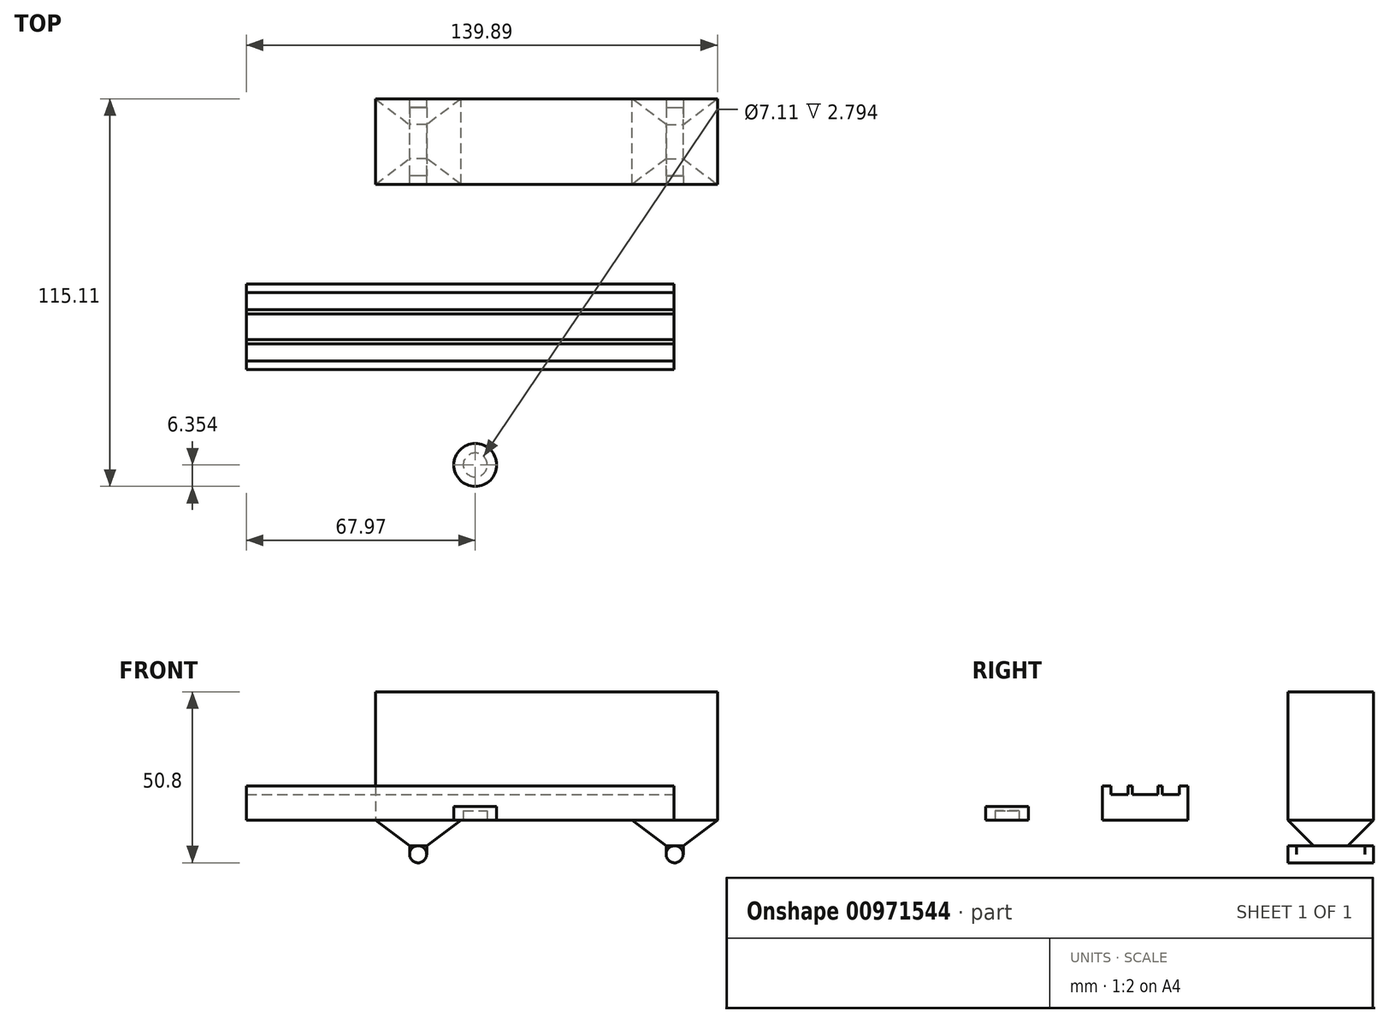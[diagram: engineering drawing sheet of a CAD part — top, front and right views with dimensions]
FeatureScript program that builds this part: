
annotation { "Feature Type Name" : "Feature", "Feature Type Description" : "" }
export const myFeature = defineFeature(function(context is Context, id is Id, definition is map)
    precondition{}
    {
        {
            var Q0;
            Q0=qCreatedBy(makeId("Top.planeOp"),FACE);
            var sketch = newSketch(context, id + "F0", { "sketchPlane" : qUnion([Q0])});
            skLineSegment(sketch, "E0.bottom", {"start": v(-67.97, 12.42) * mm, "end": v(59.03, 12.42) * mm});
            skLineSegment(sketch, "E0.top", {"start": v(-67.97, -12.98) * mm, "end": v(59.03, -12.98) * mm});
            skLineSegment(sketch, "E0.left", {"start": v(-67.97, 12.42) * mm, "end": v(-67.97, -12.98) * mm});
            skLineSegment(sketch, "E0.right", {"start": v(59.03, 12.42) * mm, "end": v(59.03, -12.98) * mm});
            skSolve(sketch);
        }
        {
            var Q0;
            Q0=makeQuery(id+"F0.imprint","IMPRINT",FACE,{"disambiguationData":[TD([[makeQuery(id+"F0.imprint","IMPRINT",EDGE,{"derivedFrom":sQuery(id+"F0.wireOp",EDGE,"E0.bottom")}),-1.0]])]});
            extrude(context, id + "F1", {"entities" : qUnion([Q0]), "depth" : 7.62 * mm, "offsetDistance" : 25.4 * mm});
        }
        {
            var Q0;
            Q0=makeQuery(id+"F1.opExtrude","CAP_FACE",FACE,{"disambiguationData":[OSD([sQuery(id+"F0.wireOp",EDGE,"E0.bottom"),sQuery(id+"F0.wireOp",EDGE,"E0.top"),sQuery(id+"F0.wireOp",EDGE,"E0.left"),sQuery(id+"F0.wireOp",EDGE,"E0.right")])],"isStart":false});
            var sketch = newSketch(context, id + "F2", { "sketchPlane" : qUnion([Q0])});
            skLineSegment(sketch, "E1", {"start": v(-67.97, 9.88) * mm, "end": v(59.03, 9.88) * mm});
            skLineSegment(sketch, "E2", {"start": v(-67.97, -10.44) * mm, "end": v(59.03, -10.44) * mm});
            skLineSegment(sketch, "E3", {"start": v(-67.97, -5.36) * mm, "end": v(59.03, -5.36) * mm});
            skLineSegment(sketch, "E4", {"start": v(-67.97, 4.8) * mm, "end": v(59.03, 4.8) * mm});
            skLineSegment(sketch, "E5", {"start": v(-67.97, -4.1) * mm, "end": v(59.03, -4.1) * mm});
            skLineSegment(sketch, "E6", {"start": v(-67.97, 3.53) * mm, "end": v(59.03, 3.53) * mm});
            skSolve(sketch);
        }
        {
            var Q0;
            {var subQ0=sQuery(id+"F2.wireOp",EDGE,"E4");Q0=makeQuery(id+"F2.imprint","IMPRINT",FACE,{"disambiguationData":[TD([[makeQuery(id+"F2.imprint","IMPRINT",EDGE,{"derivedFrom":subQ0}),-1.0]])]});}
            var Q1;
            {var subQ0=sQuery(id+"F2.wireOp",EDGE,"E1");Q1=makeQuery(id+"F2.imprint","IMPRINT",FACE,{"disambiguationData":[TD([[makeQuery(id+"F2.imprint","IMPRINT",EDGE,{"derivedFrom":subQ0}),1.0]])]});}
            var Q2;
            {var subQ0=sQuery(id+"F2.wireOp",EDGE,"E3");Q2=makeQuery(id+"F2.imprint","IMPRINT",FACE,{"disambiguationData":[TD([[makeQuery(id+"F2.imprint","IMPRINT",EDGE,{"derivedFrom":subQ0}),1.0]])]});}
            var Q3;
            {var subQ0=sQuery(id+"F2.wireOp",EDGE,"E2");Q3=makeQuery(id+"F2.imprint","IMPRINT",FACE,{"disambiguationData":[TD([[makeQuery(id+"F2.imprint","IMPRINT",EDGE,{"derivedFrom":subQ0}),-1.0]])]});}
            extrude(context, id + "F3", {"entities" : qUnion([Q0, Q1, Q2, Q3]), "operationType" : NewBodyOperationType.ADD, "depth" : 2.54 * mm, "offsetDistance" : 25.4 * mm});
        }
        {
            var Q0;
            Q0=qCreatedBy(makeId("Top.planeOp"),FACE);
            var sketch = newSketch(context, id + "F4", { "sketchPlane" : qUnion([Q0])});
            skLineSegment(sketch, "E7.bottom", {"start": v(-29.68, 67.43) * mm, "end": v(71.92, 67.43) * mm});
            skLineSegment(sketch, "E7.top", {"start": v(-29.68, 42.03) * mm, "end": v(71.92, 42.03) * mm});
            skLineSegment(sketch, "E7.left", {"start": v(-29.68, 67.43) * mm, "end": v(-29.68, 42.03) * mm});
            skLineSegment(sketch, "E7.right", {"start": v(71.92, 67.43) * mm, "end": v(71.92, 42.03) * mm});
            skSolve(sketch);
        }
        {
            var Q0;
            Q0=makeQuery(id+"F4.imprint","IMPRINT",FACE,{"disambiguationData":[TD([[makeQuery(id+"F4.imprint","IMPRINT",EDGE,{"derivedFrom":sQuery(id+"F4.wireOp",EDGE,"E7.bottom")}),-1.0]])]});
            extrude(context, id + "F5", {"entities" : qUnion([Q0]), "depth" : 38.1 * mm, "offsetDistance" : 25.4 * mm});
        }
        {
            var Q0;
            Q0=makeQuery(id+"F5.opExtrude","CAP_FACE",FACE,{"disambiguationData":[OSD([sQuery(id+"F4.wireOp",EDGE,"E7.bottom"),sQuery(id+"F4.wireOp",EDGE,"E7.top"),sQuery(id+"F4.wireOp",EDGE,"E7.left"),sQuery(id+"F4.wireOp",EDGE,"E7.right")])],"isStart":true});
            var sketch = newSketch(context, id + "F6", { "sketchPlane" : qUnion([Q0])});
            skLineSegment(sketch, "E8", {"start": v(46.52, -42.03) * mm, "end": v(46.52, -67.43) * mm});
            skLineSegment(sketch, "E9", {"start": v(-4.28, -42.03) * mm, "end": v(-4.28, -67.43) * mm});
            skSolve(sketch);
        }
        {
            var Q0;
            Q0=qCreatedBy(makeId("Top.planeOp"),FACE);
            cPlane(context, id + "F7", {"entities" : qUnion([Q0]), "cplaneType" : CPlaneType.OFFSET, "offset" : 7.62 * mm, "oppositeDirection" : true, "width" : 152.4 * mm, "height" : 152.4 * mm});
        }
        {
            var Q0;
            Q0=qCreatedBy(id+"F7.planeOp",FACE);
            var sketch = newSketch(context, id + "F8", { "sketchPlane" : qUnion([Q0])});
            skLineSegment(sketch, "E10.bottom", {"start": v(-14.44, 49.65) * mm, "end": v(-19.52, 49.65) * mm});
            skLineSegment(sketch, "E10.top", {"start": v(-14.44, 59.8) * mm, "end": v(-19.52, 59.8) * mm});
            skLineSegment(sketch, "E10.left", {"start": v(-19.52, 49.65) * mm, "end": v(-19.52, 59.8) * mm});
            skLineSegment(sketch, "E10.right", {"start": v(-14.44, 49.65) * mm, "end": v(-14.44, 59.8) * mm});
            skLineSegment(sketch, "E11.bottom", {"start": v(56.68, 49.65) * mm, "end": v(61.76, 49.65) * mm});
            skLineSegment(sketch, "E11.top", {"start": v(56.68, 59.8) * mm, "end": v(61.76, 59.8) * mm});
            skLineSegment(sketch, "E11.left", {"start": v(56.68, 49.65) * mm, "end": v(56.68, 59.8) * mm});
            skLineSegment(sketch, "E11.right", {"start": v(61.76, 49.65) * mm, "end": v(61.76, 59.8) * mm});
            skSolve(sketch);
        }
        {
            var Q1;
            {var subQ0=sQuery(id+"F6.wireOp",EDGE,"E9");Q1=makeQuery(id+"F6.imprint","IMPRINT",FACE,{"disambiguationData":[TD([[makeQuery(id+"F6.imprint","IMPRINT",EDGE,{"derivedFrom":subQ0}),-1.0]])]});}
            var Q2;
            Q2=makeQuery(id+"F8.imprint","IMPRINT",FACE,{"disambiguationData":[TD([[makeQuery(id+"F8.imprint","IMPRINT",EDGE,{"derivedFrom":sQuery(id+"F8.wireOp",EDGE,"E10.bottom")}),-1.0]])]});
            loft(context, id + "F9", {"operationType" : NewBodyOperationType.ADD, "sheetProfilesArray" : [{ "sheetProfileEntities" : qUnion([Q1]) }, { "sheetProfileEntities" : qUnion([Q2]) }]});
        }
        {
            var Q1;
            Q1=makeQuery(id+"F8.imprint","IMPRINT",FACE,{"disambiguationData":[TD([[makeQuery(id+"F8.imprint","IMPRINT",EDGE,{"derivedFrom":sQuery(id+"F8.wireOp",EDGE,"E11.bottom")}),1.0]])]});
            var Q2;
            {var subQ0=sQuery(id+"F6.wireOp",EDGE,"E8");Q2=makeQuery(id+"F6.imprint","IMPRINT",FACE,{"disambiguationData":[TD([[makeQuery(id+"F6.imprint","IMPRINT",EDGE,{"derivedFrom":subQ0}),1.0]])]});}
            loft(context, id + "F10", {"operationType" : NewBodyOperationType.ADD, "sheetProfilesArray" : [{ "sheetProfileEntities" : qUnion([Q1]) }, { "sheetProfileEntities" : qUnion([Q2]) }]});
        }
        {
            var Q0;
            Q0=makeQuery(id+"F10.opLoft","CAP_FACE",FACE,{"disambiguationData":[OSD([makeQuery(id+"F8.imprint","IMPRINT",FACE,{"disambiguationData":[TD([[makeQuery(id+"F8.imprint","IMPRINT",EDGE,{"derivedFrom":sQuery(id+"F8.wireOp",EDGE,"E11.bottom")}),1.0]])]})])],"isStart":true});
            var Q1;
            Q1=makeQuery(id+"F9.opLoft","CAP_FACE",FACE,{"disambiguationData":[OSD([makeQuery(id+"F8.imprint","IMPRINT",FACE,{"disambiguationData":[TD([[makeQuery(id+"F8.imprint","IMPRINT",EDGE,{"derivedFrom":sQuery(id+"F8.wireOp",EDGE,"E10.bottom")}),-1.0]])]})])],"isStart":true});
            extrude(context, id + "F11", {"entities" : qUnion([Q0, Q1]), "operationType" : NewBodyOperationType.ADD, "depth" : 5.08 * mm, "offsetDistance" : 25.4 * mm});
        }
        {
            var Q0;
            Q0=makeQuery(id+"F11.opExtrude","CAP_EDGE",EDGE,{"disambiguationData":[OSD([sQuery(id+"F8.wireOp",EDGE,"E11.bottom"),sQuery(id+"F8.wireOp",EDGE,"E11.top"),sQuery(id+"F8.wireOp",EDGE,"E11.right")])],"isStart":false});
            var Q1;
            Q1=makeQuery(id+"F11.opExtrude","CAP_EDGE",EDGE,{"disambiguationData":[OSD([sQuery(id+"F8.wireOp",EDGE,"E11.bottom"),sQuery(id+"F8.wireOp",EDGE,"E11.top"),sQuery(id+"F8.wireOp",EDGE,"E11.left")])],"isStart":false});
            var Q2;
            Q2=makeQuery(id+"F11.opExtrude","CAP_EDGE",EDGE,{"disambiguationData":[OSD([sQuery(id+"F8.wireOp",EDGE,"E10.bottom"),sQuery(id+"F8.wireOp",EDGE,"E10.top"),sQuery(id+"F8.wireOp",EDGE,"E10.left")])],"isStart":false});
            var Q3;
            Q3=makeQuery(id+"F11.opExtrude","CAP_EDGE",EDGE,{"disambiguationData":[OSD([sQuery(id+"F8.wireOp",EDGE,"E10.bottom"),sQuery(id+"F8.wireOp",EDGE,"E10.top"),sQuery(id+"F8.wireOp",EDGE,"E10.right")])],"isStart":false});
            fillet(context, id + "F12", {"entities" : qUnion([Q0, Q1, Q2, Q3]), "radius" : 2.54 * mm, "tangentPropagation" : true, "allowEdgeOverflow" : false});
        }
        {
            var Q0;
            Q0=makeQuery(id+"F11.opExtrude","SWEPT_FACE",FACE,{"disambiguationData":[OSD([sQuery(id+"F8.wireOp",EDGE,"E10.top"),sQuery(id+"F8.wireOp",EDGE,"E10.left"),sQuery(id+"F8.wireOp",EDGE,"E10.right")])]});
            var Q1;
            Q1=makeQuery(id+"F11.opExtrude","SWEPT_FACE",FACE,{"disambiguationData":[OSD([sQuery(id+"F8.wireOp",EDGE,"E11.top"),sQuery(id+"F8.wireOp",EDGE,"E11.left"),sQuery(id+"F8.wireOp",EDGE,"E11.right")])]});
            extrude(context, id + "F13", {"entities" : qUnion([Q0, Q1]), "operationType" : NewBodyOperationType.ADD, "depth" : 5.08 * mm, "offsetDistance" : 25.4 * mm});
        }
        {
            var Q0;
            Q0=makeQuery(id+"F11.opExtrude","SWEPT_FACE",FACE,{"disambiguationData":[OSD([sQuery(id+"F8.wireOp",EDGE,"E10.bottom"),sQuery(id+"F8.wireOp",EDGE,"E10.left"),sQuery(id+"F8.wireOp",EDGE,"E10.right")])]});
            var Q1;
            Q1=makeQuery(id+"F11.opExtrude","SWEPT_FACE",FACE,{"disambiguationData":[OSD([sQuery(id+"F8.wireOp",EDGE,"E11.bottom"),sQuery(id+"F8.wireOp",EDGE,"E11.left"),sQuery(id+"F8.wireOp",EDGE,"E11.right")])]});
            extrude(context, id + "F14", {"entities" : qUnion([Q0, Q1]), "operationType" : NewBodyOperationType.ADD, "depth" : 5.08 * mm, "offsetDistance" : 25.4 * mm});
        }
        {
            var Q0;
            Q0=makeQuery(id+"F13.opExtrude","CAP_FACE",FACE,{"disambiguationData":[OSD([sQuery(id+"F8.wireOp",EDGE,"E11.top"),sQuery(id+"F8.wireOp",EDGE,"E11.left"),sQuery(id+"F8.wireOp",EDGE,"E11.right")])],"isStart":false});
            var sketch = newSketch(context, id + "F15", { "sketchPlane" : qUnion([Q0])});
            skCircle(sketch, "E12", {"center": v(-59.22, -10.16) * mm, "radius": 2.54 * mm});
            skSolve(sketch);
        }
        {
            var Q0;
            Q0=makeQuery(id+"F13.opExtrude","CAP_FACE",FACE,{"disambiguationData":[OSD([sQuery(id+"F8.wireOp",EDGE,"E10.top"),sQuery(id+"F8.wireOp",EDGE,"E10.left"),sQuery(id+"F8.wireOp",EDGE,"E10.right")])],"isStart":false});
            var sketch = newSketch(context, id + "F16", { "sketchPlane" : qUnion([Q0])});
            skCircle(sketch, "E13", {"center": v(16.98, -10.16) * mm, "radius": 2.54 * mm});
            skSolve(sketch);
        }
        {
            var Q0;
            {var subQ0=sQuery(id+"F16.wireOp",EDGE,"E13");var subQ2=sQuery(id+"F8.wireOp",EDGE,"E10.top");var subQ4=sQuery(id+"F8.wireOp",EDGE,"E10.right");var subQ6=makeQuery(id+"F16.imprint","INTERSECT",VERTEX,{"derivedFrom":[makeQuery(id+"F13.opExtrude","CAP_EDGE",EDGE,{"disambiguationData":[OSD([subQ2,subQ4])],"isStart":false}),subQ0]});Q0=makeQuery(id+"F16.imprint","IMPRINT",FACE,{"disambiguationData":[TD([[makeQuery(id+"F16.imprint","IMPRINT",EDGE,{"disambiguationData":[TD([[subQ6,-1.0]])],"derivedFrom":subQ0}),1.0]])]});}
            var Q1;
            {var subQ0=sQuery(id+"F15.wireOp",EDGE,"E12");var subQ1=sQuery(id+"F8.wireOp",EDGE,"E11.left");var subQ2=sQuery(id+"F8.wireOp",EDGE,"E11.top");var subQ3=makeQuery(id+"F15.imprint","INTERSECT",VERTEX,{"derivedFrom":[makeQuery(id+"F13.opExtrude","CAP_EDGE",EDGE,{"disambiguationData":[OSD([subQ2,subQ1])],"isStart":false}),subQ0]});Q1=makeQuery(id+"F15.imprint","IMPRINT",FACE,{"disambiguationData":[TD([[makeQuery(id+"F15.imprint","IMPRINT",EDGE,{"disambiguationData":[TD([[subQ3,1.0]])],"derivedFrom":subQ0}),1.0]])]});}
            extrude(context, id + "F17", {"entities" : qUnion([Q0, Q1]), "operationType" : NewBodyOperationType.ADD, "depth" : 2.54 * mm, "offsetDistance" : 25.4 * mm});
        }
        {
            var Q0;
            Q0=makeQuery(id+"F14.opExtrude","CAP_FACE",FACE,{"disambiguationData":[OSD([sQuery(id+"F8.wireOp",EDGE,"E10.bottom"),sQuery(id+"F8.wireOp",EDGE,"E10.left"),sQuery(id+"F8.wireOp",EDGE,"E10.right")])],"isStart":false});
            var sketch = newSketch(context, id + "F18", { "sketchPlane" : qUnion([Q0])});
            skCircle(sketch, "E14", {"center": v(-16.98, -10.16) * mm, "radius": 2.54 * mm});
            skSolve(sketch);
        }
        {
            var Q0;
            Q0=makeQuery(id+"F14.opExtrude","CAP_FACE",FACE,{"disambiguationData":[OSD([sQuery(id+"F8.wireOp",EDGE,"E11.bottom"),sQuery(id+"F8.wireOp",EDGE,"E11.left"),sQuery(id+"F8.wireOp",EDGE,"E11.right")])],"isStart":false});
            var sketch = newSketch(context, id + "F19", { "sketchPlane" : qUnion([Q0])});
            skCircle(sketch, "E15", {"center": v(59.22, -10.16) * mm, "radius": 2.54 * mm});
            skSolve(sketch);
        }
        {
            var Q0;
            {var subQ0=sQuery(id+"F19.wireOp",EDGE,"E15");var subQ2=sQuery(id+"F8.wireOp",EDGE,"E11.bottom");var subQ4=sQuery(id+"F8.wireOp",EDGE,"E11.left");var subQ6=makeQuery(id+"F19.imprint","INTERSECT",VERTEX,{"derivedFrom":[makeQuery(id+"F14.opExtrude","CAP_EDGE",EDGE,{"disambiguationData":[OSD([subQ2,subQ4])],"isStart":false}),subQ0]});Q0=makeQuery(id+"F19.imprint","IMPRINT",FACE,{"disambiguationData":[TD([[makeQuery(id+"F19.imprint","IMPRINT",EDGE,{"disambiguationData":[TD([[subQ6,-1.0]])],"derivedFrom":subQ0}),1.0]])]});}
            var Q1;
            {var subQ0=sQuery(id+"F18.wireOp",EDGE,"E14");var subQ1=sQuery(id+"F8.wireOp",EDGE,"E10.right");var subQ2=sQuery(id+"F8.wireOp",EDGE,"E10.bottom");var subQ3=makeQuery(id+"F18.imprint","INTERSECT",VERTEX,{"derivedFrom":[makeQuery(id+"F14.opExtrude","CAP_EDGE",EDGE,{"disambiguationData":[OSD([subQ2,subQ1])],"isStart":false}),subQ0]});Q1=makeQuery(id+"F18.imprint","IMPRINT",FACE,{"disambiguationData":[TD([[makeQuery(id+"F18.imprint","IMPRINT",EDGE,{"disambiguationData":[TD([[subQ3,1.0]])],"derivedFrom":subQ0}),1.0]])]});}
            extrude(context, id + "F20", {"entities" : qUnion([Q0, Q1]), "operationType" : NewBodyOperationType.ADD, "depth" : 2.54 * mm, "offsetDistance" : 25.4 * mm});
        }
        {
            var Q0;
            Q0=qCreatedBy(makeId("Top.planeOp"),FACE);
            var sketch = newSketch(context, id + "F21", { "sketchPlane" : qUnion([Q0])});
            skCircle(sketch, "E16", {"center": v(0, -41.33) * mm, "radius": 6.35 * mm});
            skSolve(sketch);
        }
        {
            var Q0;
            Q0=makeQuery(id+"F21.imprint","IMPRINT",FACE,{"disambiguationData":[TD([[makeQuery(id+"F21.imprint","IMPRINT",EDGE,{"derivedFrom":sQuery(id+"F21.wireOp",EDGE,"E16")}),1.0]])]});
            extrude(context, id + "F22", {"entities" : qUnion([Q0]), "depth" : 4.06 * mm, "offsetDistance" : 25.4 * mm});
        }
        {
            var Q0;
            Q0=makeQuery(id+"F22.opExtrude","CAP_FACE",FACE,{"disambiguationData":[OSD([sQuery(id+"F21.wireOp",EDGE,"E16")])],"isStart":true});
            var sketch = newSketch(context, id + "F23", { "sketchPlane" : qUnion([Q0])});
            skCircle(sketch, "E17", {"center": v(0, 41.33) * mm, "radius": 3.56 * mm});
            skSolve(sketch);
        }
        {
            var Q0;
            Q0=makeQuery(id+"F23.imprint","IMPRINT",FACE,{"disambiguationData":[TD([[makeQuery(id+"F23.imprint","IMPRINT",EDGE,{"derivedFrom":sQuery(id+"F23.wireOp",EDGE,"E17")}),1.0]])]});
            extrude(context, id + "F24", {"entities" : qUnion([Q0]), "operationType" : NewBodyOperationType.REMOVE, "oppositeDirection" : true, "depth" : 2.8 * mm, "offsetDistance" : 25.4 * mm});
        }
    });
